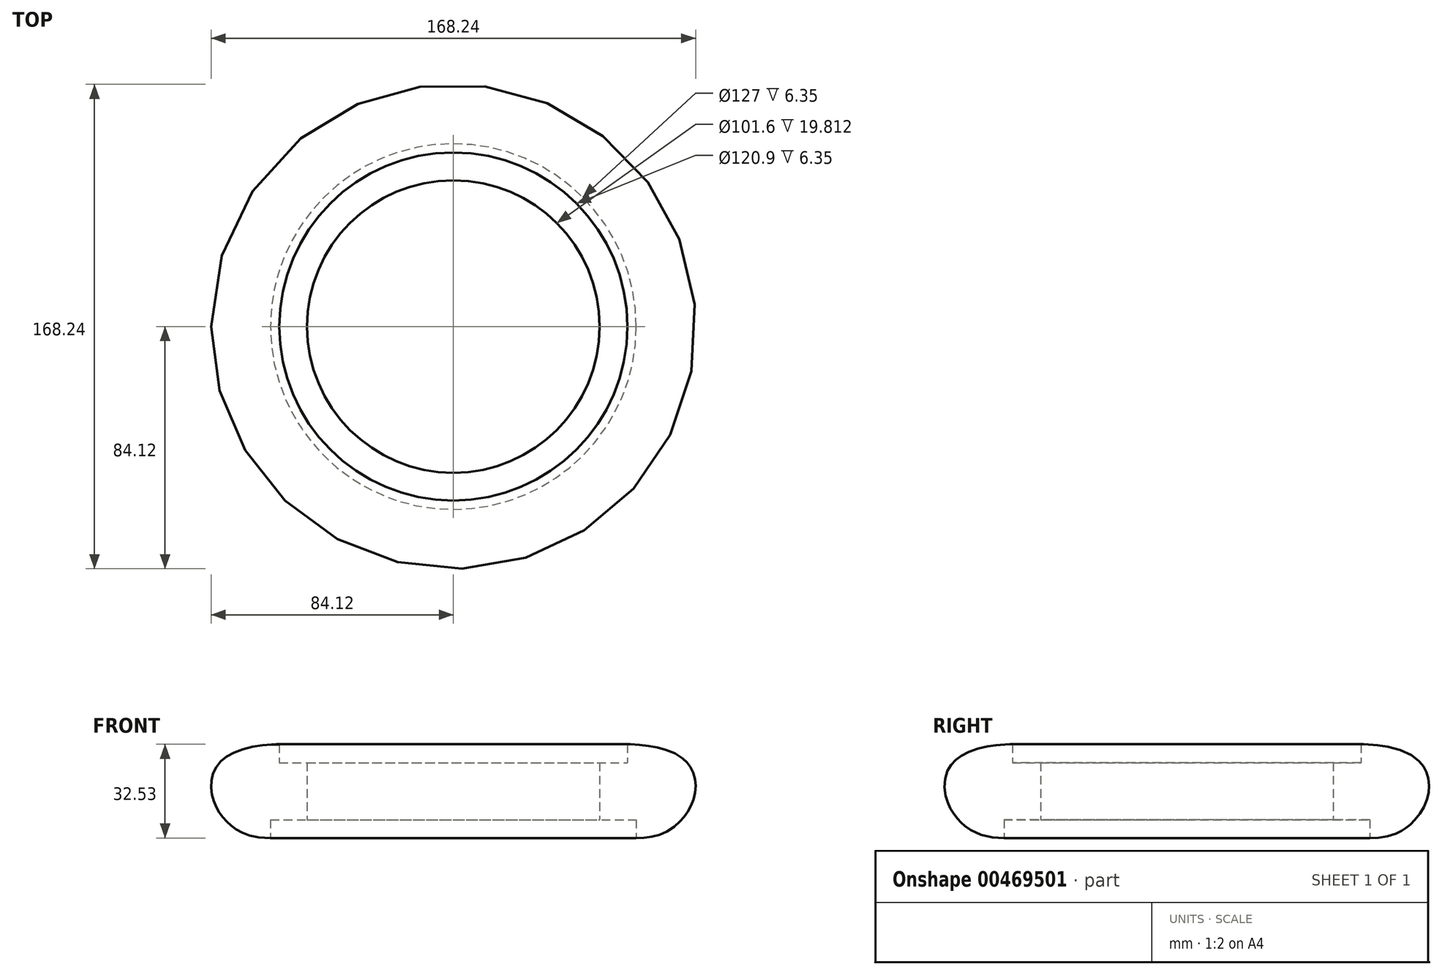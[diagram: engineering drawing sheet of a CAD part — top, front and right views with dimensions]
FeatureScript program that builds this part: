
annotation { "Feature Type Name" : "Feature", "Feature Type Description" : "" }
export const myFeature = defineFeature(function(context is Context, id is Id, definition is map)
    precondition{}
    {
        {
            var Q0;
            Q0=qCreatedBy(makeId("Front.planeOp"),FACE);
            var sketch = newSketch(context, id + "F0", { "sketchPlane" : qUnion([Q0])});
            skLineSegment(sketch, "E0", {"start": v(0, 0) * mm, "end": v(-63.5, 0) * mm, "construction": true});
            skLineSegment(sketch, "E1", {"start": v(0, 0) * mm, "end": v(0, 31.75) * mm, "construction": true});
            skLineSegment(sketch, "E2", {"start": v(-63.5, 0) * mm, "end": v(-63.5, 31.75) * mm, "construction": true});
            skLineSegment(sketch, "E3", {"start": v(-63.5, 31.75) * mm, "end": v(-69.85, 31.75) * mm, "construction": true});
            skLineSegment(sketch, "E4", {"start": v(-69.85, 31.75) * mm, "end": v(-69.85, 25.4) * mm, "construction": true});
            skLineSegment(sketch, "E5", {"start": v(-69.85, 25.4) * mm, "end": v(-69.85, 6.35) * mm, "construction": true});
            skLineSegment(sketch, "E6", {"start": v(-69.85, 6.35) * mm, "end": v(-69.85, 0) * mm, "construction": true});
            skSolve(sketch);
        }
        {
            var Q0;
            Q0=qCreatedBy(makeId("Front.planeOp"),FACE);
            var sketch = newSketch(context, id + "F1", { "sketchPlane" : qUnion([Q0])});
            skLineSegment(sketch, "E7", {"start": v(-60.45, 26.16) * mm, "end": v(-50.8, 26.16) * mm});
            skLineSegment(sketch, "E8", {"start": v(-60.45, 26.16) * mm, "end": v(-60.45, 32.51) * mm});
            skLineSegment(sketch, "E9", {"start": v(-63.5, 0) * mm, "end": v(-63.5, 6.35) * mm});
            skLineSegment(sketch, "E10", {"start": v(-63.5, 6.35) * mm, "end": v(-50.8, 6.35) * mm});
            skLineSegment(sketch, "E11", {"start": v(-50.8, 6.35) * mm, "end": v(-50.8, 26.16) * mm});
            skFitSpline(sketch, "E12", {"points": [v(-60.45, 32.51) * mm, v(-75.34, 30.06) * mm, v(-83.1, 23.24) * mm, v(-83.72, 14.55) * mm, v(-80.66, 8) * mm, v(-76.16, 3.51) * mm, v(-63.5, 0) * mm], "startDerivative": vector(-54.07, 2.17) * mm, "endDerivative": vector(103.7, 0) * mm});
            skSolve(sketch);
        }
        {
            var Q0;
            Q0=makeQuery(id+"F1.imprint","IMPRINT",FACE,{"disambiguationData":[TD([[makeQuery(id+"F1.imprint","IMPRINT",EDGE,{"derivedFrom":sQuery(id+"F1.wireOp",EDGE,"E7")}),-1.0]])]});
            var Q1;
            Q1=sQuery(id+"F0.wireOp",EDGE,"E1");
            revolve(context, id + "F2", {"entities" : qUnion([Q0]), "axis" : qUnion([Q1]), "revolveType" : RevolveType.FULL});
        }
    });
